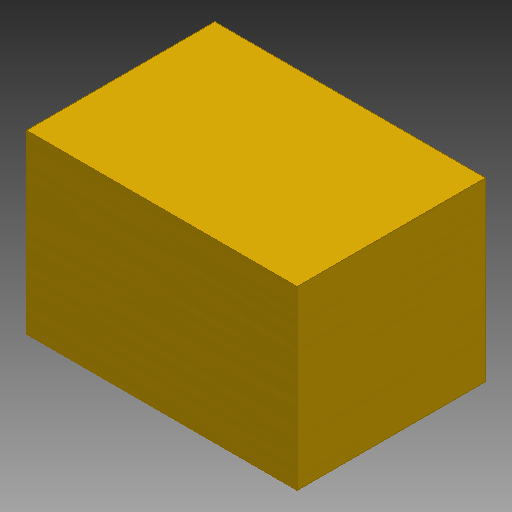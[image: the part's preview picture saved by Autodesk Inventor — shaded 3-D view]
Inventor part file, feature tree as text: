
AUTODESK INVENTOR PART (.ipt)
format: ipt  version: 2017 (Build 210142000, 142)  size: 95,744 bytes
history: native  units: mm
features: other x4, reference x2, extrude x1, sketch x1
ambient origin geometry x8: Origin, YZ Plane, XZ Plane, XY Plane, X Axis, Y Axis, Z Axis, Center Point
bodies: Solid1 (feature_tree)
feature tree (8):
  extrude  "Extrusion1"  Depth=150.0mm TaperAngle=0.0deg
  sketch  "Sketch1"  dims[d0=230.0mm d1=150.0mm d2=0.0mm]
  reference  "Reference1"
  reference  "Reference2"
  other  "<userpath>\OneDrive\Inventor\VolledigGeassembleerdv001.iam"
  other  "VolledigGeassembleerdv001.iam"
  other  "Frame:1"
  other  "aandrijfMotor:1"
